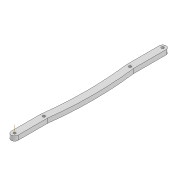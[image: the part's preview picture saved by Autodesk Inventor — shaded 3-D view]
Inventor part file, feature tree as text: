
AUTODESK INVENTOR PART (.ipt)
format: ipt  version: 2022 (Build 260153000, 153)  size: 101,888 bytes
history: native  units: mm
features: extrude x1, other x1, sketch x1
ambient origin geometry x8: Origin, YZ Plane, XZ Plane, XY Plane, X Axis, Y Axis, Z Axis, Center Point
bodies: Solid1 (feature_tree)
feature tree (3):
  extrude  "Extrusion1"  Depth=300.0mm
  other  "Work Axis2"
  sketch  "Sketch1"  dims[d0=2.2mm d1=2.2mm d2=6.0mm d3=129.784mm d4=2.2mm d5=25.613mm d6=4.0mm d7=0.0mm d8=2.2mm d9=101.165mm d10=300.0mm d11=300.0mm]
